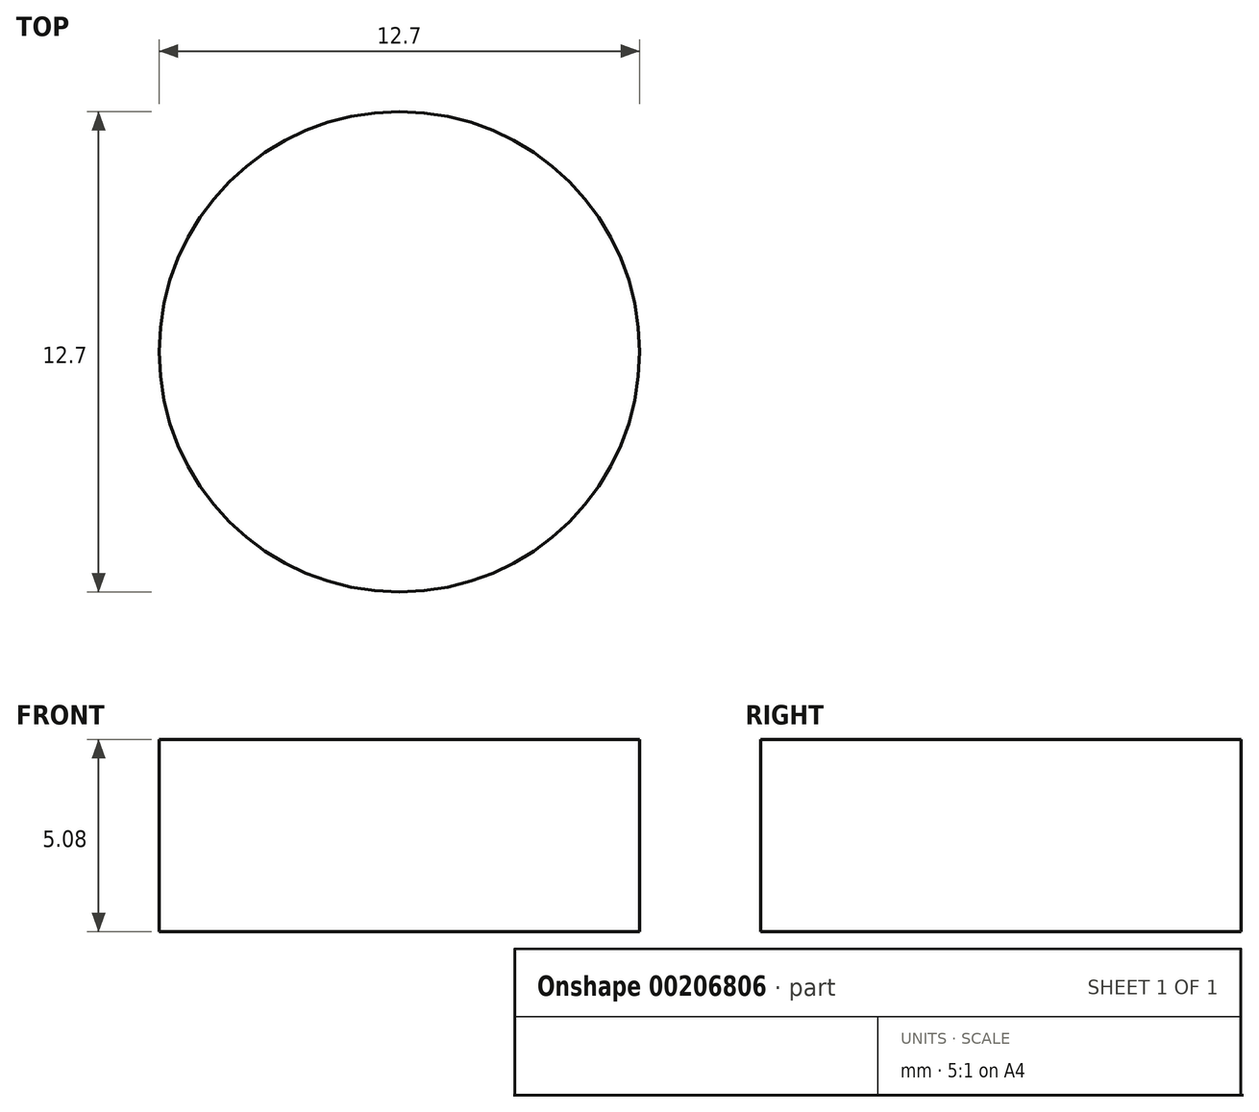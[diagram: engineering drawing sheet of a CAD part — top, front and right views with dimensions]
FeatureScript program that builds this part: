
annotation { "Feature Type Name" : "Feature", "Feature Type Description" : "" }
export const myFeature = defineFeature(function(context is Context, id is Id, definition is map)
    precondition{}
    {
        {
            var Q0;
            Q0=qCreatedBy(makeId("Top.planeOp"),FACE);
            var sketch = newSketch(context, id + "F0", { "sketchPlane" : qUnion([Q0])});
            skCircle(sketch, "E0", {"center": v(0, 0) * mm, "radius": 6.35 * mm});
            skSolve(sketch);
        }
        {
            var Q0;
            Q0=sQuery(id+"F0.wireOp",EDGE,"E0");
            extrude(context, id + "F1", {"bodyType" : ToolBodyType.SURFACE, "surfaceEntities" : qUnion([Q0]), "depth" : 5.08 * mm});
        }
    });
